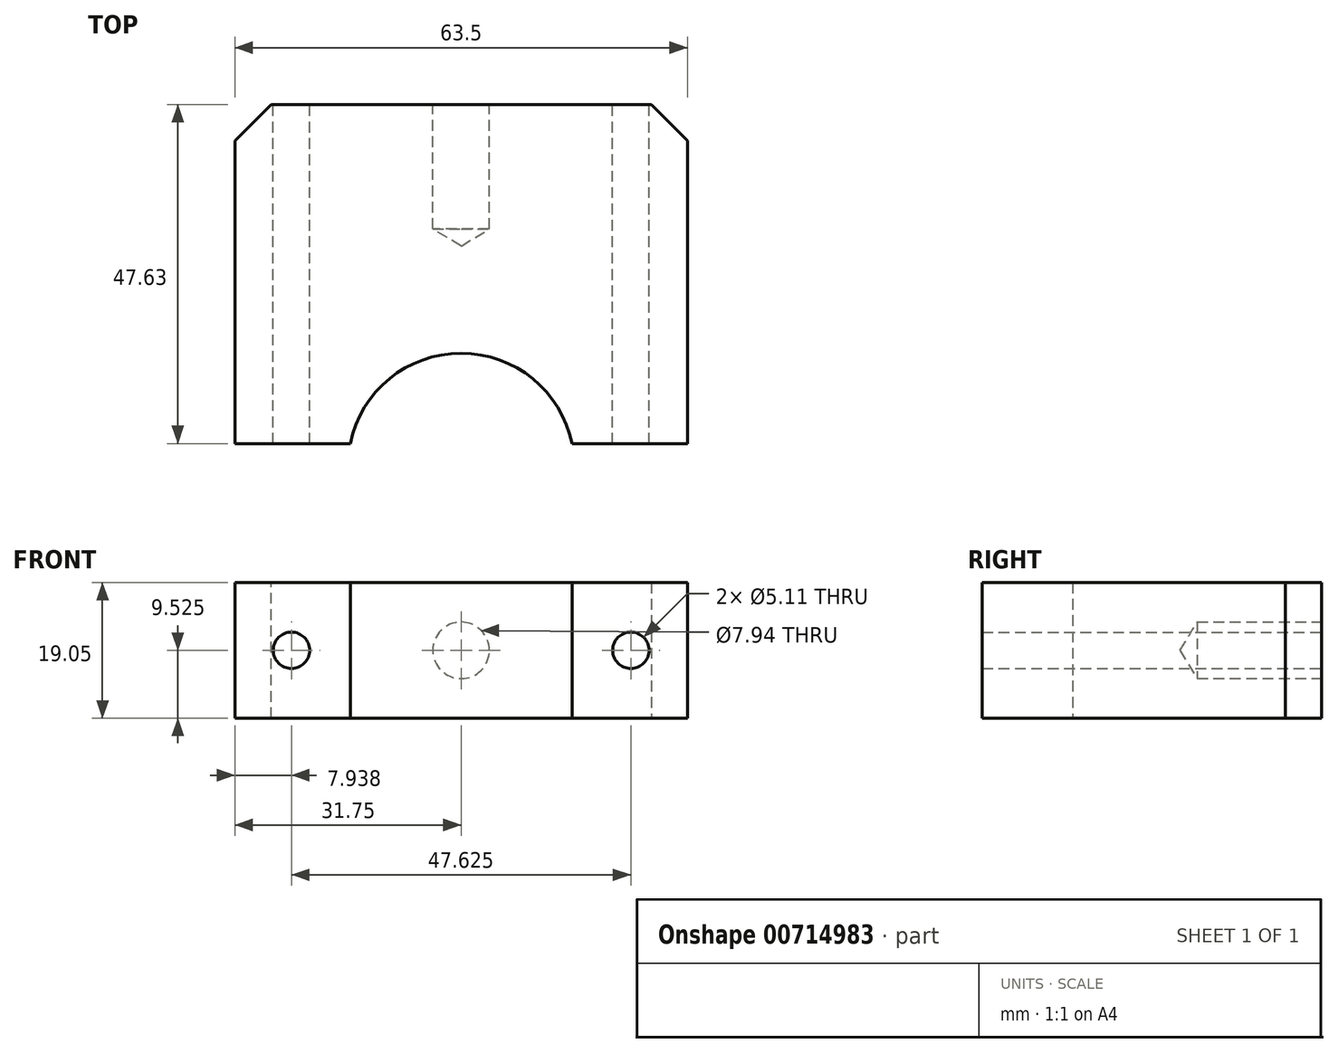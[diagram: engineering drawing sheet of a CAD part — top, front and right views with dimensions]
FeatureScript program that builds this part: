
annotation { "Feature Type Name" : "Feature", "Feature Type Description" : "" }
export const myFeature = defineFeature(function(context is Context, id is Id, definition is map)
    precondition{}
    {
        {
            var Q0;
            Q0=qCreatedBy(makeId("Top.planeOp"),FACE);
            var sketch = newSketch(context, id + "F0", { "sketchPlane" : qUnion([Q0])});
            skLineSegment(sketch, "E0.bottom", {"start": v(0, 0) * mm, "end": v(15.88, 0) * mm});
            skLineSegment(sketch, "E0.top", {"start": v(0, 50.8) * mm, "end": v(63.5, 50.8) * mm});
            skLineSegment(sketch, "E0.left", {"start": v(0, 0) * mm, "end": v(0, 50.8) * mm});
            skLineSegment(sketch, "E0.right", {"start": v(63.5, 0) * mm, "end": v(63.5, 50.8) * mm});
            skArc(sketch, "E1", {"start": v(47.62, 0) * mm, "mid": v(31.75, 15.88) * mm, "end": v(15.88, 0) * mm});
            skLineSegment(sketch, "E2.trimOffspring", {"start": v(47.62, 0) * mm, "end": v(63.5, 0) * mm});
            skSolve(sketch);
        }
        {
            var Q0;
            Q0=makeQuery(id+"F0.imprint","IMPRINT",FACE,{"disambiguationData":[TD([[makeQuery(id+"F0.imprint","IMPRINT",EDGE,{"derivedFrom":sQuery(id+"F0.wireOp",EDGE,"E0.bottom")}),1.0]])]});
            extrude(context, id + "F1", {"entities" : qUnion([Q0]), "depth" : 19.05 * mm, "offsetDistance" : 25.4 * mm});
        }
        {
            var Q0;
            Q0=makeQuery(id+"F1.opExtrude","SWEPT_FACE",FACE,{"disambiguationData":[OSD([sQuery(id+"F0.wireOp",EDGE,"E0.top")])]});
            var sketch = newSketch(context, id + "F2", { "sketchPlane" : qUnion([Q0])});
            skLineSegment(sketch, "E3", {"start": v(-63.5, 9.53) * mm, "end": v(-47.62, 9.53) * mm, "construction": true});
            skLineSegment(sketch, "E4", {"start": v(-31.75, 19.05) * mm, "end": v(-31.75, 0) * mm, "construction": true});
            skPoint(sketch, "E5", {"position": v(-55.56, 9.53) * mm});
            skPoint(sketch, "E6", {"position": v(-7.94, 9.53) * mm});
            skLineSegment(sketch, "E7.0", {"start": v(-47.62, 19.05) * mm, "end": v(-47.62, 0) * mm, "construction": true});
            skLineSegment(sketch, "E8.0", {"start": v(-15.88, 19.05) * mm, "end": v(-15.88, 0) * mm, "construction": true});
            skLineSegment(sketch, "E9.trimOffspring", {"start": v(-15.88, 9.53) * mm, "end": v(0, 9.53) * mm, "construction": true});
            skSolve(sketch);
        }
        {
            var Q0;
            Q0=sQuery(id+"F2.wireOp",VERTEX,"E5");
            var Q1;
            Q1=sQuery(id+"F2.wireOp",VERTEX,"E6");
            var Q2;
            Q2=makeQuery(id+"F1.opExtrude","SWEPT_BODY",BODY,{"disambiguationData":[OSD([sQuery(id+"F0.wireOp",EDGE,"E0.bottom"),sQuery(id+"F0.wireOp",EDGE,"E0.top"),sQuery(id+"F0.wireOp",EDGE,"E0.left"),sQuery(id+"F0.wireOp",EDGE,"E0.right"),sQuery(id+"F0.wireOp",EDGE,"E1"),sQuery(id+"F0.wireOp",EDGE,"E2.trimOffspring")])]});
            hole(context, id + "F3", {"style" : HoleStyle.SIMPLE, "endStyle" : HoleEndStyle.THROUGH, "standardTappedOrClearance" : lookupTablePath({ "standard" : "ANSI", "engagement" : "75%", "pitch" : "20 tpi", "size" : "1/4", "type" : "Tapped" }), "standardBlindInLast" : lookupTablePath({ "standard" : "ANSI", "engagement" : "75%", "pitch" : "20 tpi", "size" : "1/4", "type" : "Tapped" }), "holeDiameter" : 5.1 * mm, "majorDiameter" : 6.35 * mm, "showTappedDepth" : true, "isTappedThrough" : true, "tappedDepth" : 12.7 * mm, "tapClearance" : 3, "locations" : qUnion([Q0, Q1]), "scope" : qUnion([Q2])});
        }
        {
            var Q0;
            Q0=makeQuery(id+"F1.opExtrude","SWEPT_EDGE",EDGE,{"disambiguationData":[OSD([sQuery(id+"F0.wireOp",EDGE,"E0.top"),sQuery(id+"F0.wireOp",EDGE,"E0.right")])]});
            var Q1;
            Q1=makeQuery(id+"F1.opExtrude","SWEPT_EDGE",EDGE,{"disambiguationData":[OSD([sQuery(id+"F0.wireOp",EDGE,"E0.top"),sQuery(id+"F0.wireOp",EDGE,"E0.left")])]});
            chamfer(context, id + "F4", {"entities" : qUnion([Q0, Q1]), "width" : 5.08 * mm, "tangentPropagation" : true});
        }
        {
            var Q0;
            Q0=makeQuery(id+"F1.opExtrude","CAP_FACE",FACE,{"disambiguationData":[OSD([sQuery(id+"F0.wireOp",EDGE,"E0.bottom"),sQuery(id+"F0.wireOp",EDGE,"E0.top"),sQuery(id+"F0.wireOp",EDGE,"E0.left"),sQuery(id+"F0.wireOp",EDGE,"E0.right"),sQuery(id+"F0.wireOp",EDGE,"E1"),sQuery(id+"F0.wireOp",EDGE,"E2.trimOffspring")])],"isStart":false});
            var sketch = newSketch(context, id + "F5", { "sketchPlane" : qUnion([Q0])});
            skLineSegment(sketch, "E10.bottom", {"start": v(0, 0) * mm, "end": v(63.5, 0) * mm});
            skLineSegment(sketch, "E10.top", {"start": v(0, 3.18) * mm, "end": v(63.5, 3.18) * mm});
            skLineSegment(sketch, "E10.left", {"start": v(0, 0) * mm, "end": v(0, 3.18) * mm});
            skLineSegment(sketch, "E10.right", {"start": v(63.5, 0) * mm, "end": v(63.5, 3.18) * mm});
            skSolve(sketch);
        }
        {
            var Q0;
            {var subQ0=sQuery(id+"F5.wireOp",EDGE,"E10.left");Q0=makeQuery(id+"F5.imprint","IMPRINT",FACE,{"disambiguationData":[TD([[makeQuery(id+"F5.imprint","IMPRINT",EDGE,{"derivedFrom":subQ0}),-1.0]])]});}
            var Q1;
            {var subQ0=sQuery(id+"F5.wireOp",EDGE,"E10.right");Q1=makeQuery(id+"F5.imprint","IMPRINT",FACE,{"disambiguationData":[TD([[makeQuery(id+"F5.imprint","IMPRINT",EDGE,{"derivedFrom":subQ0}),1.0]])]});}
            extrude(context, id + "F6", {"entities" : qUnion([Q0, Q1]), "operationType" : NewBodyOperationType.REMOVE, "oppositeDirection" : true, "depth" : 25.4 * mm, "offsetDistance" : 25.4 * mm});
        }
        {
            var Q0;
            Q0=makeQuery(id+"F1.opExtrude","SWEPT_FACE",FACE,{"disambiguationData":[OSD([sQuery(id+"F0.wireOp",EDGE,"E0.top")])]});
            var sketch = newSketch(context, id + "F7", { "sketchPlane" : qUnion([Q0])});
            skLineSegment(sketch, "E11", {"start": v(-31.75, 19.05) * mm, "end": v(-31.75, 0) * mm, "construction": true});
            skPoint(sketch, "E12", {"position": v(-31.75, 9.53) * mm});
            skSolve(sketch);
        }
        {
            var Q0;
            Q0=sQuery(id+"F7.wireOp",VERTEX,"E12");
            var Q1;
            Q1=makeQuery(id+"F1.opExtrude","SWEPT_BODY",BODY,{"disambiguationData":[OSD([sQuery(id+"F0.wireOp",EDGE,"E0.bottom"),sQuery(id+"F0.wireOp",EDGE,"E0.top"),sQuery(id+"F0.wireOp",EDGE,"E0.left"),sQuery(id+"F0.wireOp",EDGE,"E0.right"),sQuery(id+"F0.wireOp",EDGE,"E1"),sQuery(id+"F0.wireOp",EDGE,"E2.trimOffspring")])]});
            hole(context, id + "F8", {"style" : HoleStyle.SIMPLE, "endStyle" : HoleEndStyle.BLIND, "standardTappedOrClearance" : lookupTablePath({ "standard" : "ANSI", "engagement" : "75%", "pitch" : "16 tpi", "size" : "3/8", "type" : "Tapped" }), "standardBlindInLast" : lookupTablePath({ "standard" : "ANSI", "engagement" : "75%", "pitch" : "16 tpi", "size" : "3/8", "type" : "Tapped" }), "holeDiameter" : 7.94 * mm, "majorDiameter" : 9.52 * mm, "showTappedDepth" : true, "holeDepth" : 17.48 * mm, "isTappedThrough" : true, "tappedDepth" : 12.71 * mm, "tapClearance" : 3, "locations" : qUnion([Q0]), "scope" : qUnion([Q1])});
        }
    });
